# Revit family: RN 92001 Optifitt-Serra-Raccordo
name_source: partatom
category: Rohrformteile
units: mm (PartAtom-declared; Revit-internal decimal feet)

## family parameters
Arbeitsebenenbasiert = Nein
Beim Laden mit Abzugskörper schneiden = Nein
Bemaßung runder Anschluss = Durchmesser verwenden
Gemeinsam genutzt = Nein
Immer vertikal = Ja
Teiletyp = Verbindung

## types (10) — shared parameters
1.010.00.2 Blattnummer der Richtlinie = 29
1.010.00.3 Ausgabedatum (Monat) der Richtlinie = 201308
1.010.00.4 Herstellername = R. Nussbaum AG
1.010.00.5 Revisionsdatum der Datei = 20190521
1.010.00.6 Webadresse des Herstellers = http://www.nussbaum.ch
1.100.00.4 Produktbezeichnung = Versorgung
1.110.00.2 Index = 3
1.110.00.4 Produktbezeichnung = Optifitt-Serra
1.960/3L.00.8 Link (URL) = https://www.nussbaum.ch
29.700.00.4 Produktname = Optifitt-Serra-Anschlussverschraubung, mit Aussengewinde
29.700.00.5 Produktkennung = 2
29.700.00.6 Querschnittsform = 1
29.700.00.7 Nennweitensystem = DN
29.700.00.8 Nenndrucksystem = PN
29.710.02.4 Nenndruck = 16
29.710.02.5 max. zul. Überdruck [hPa] = 1600
29.710.02.7 max. zul. Dauer-Betriebsdruck [hPa] = 1600
29.710.02.9 max. zul. Dauer-Betriebstemperatur [°C] = 90
Connector Visibility = Nein
EnclosingSpace Visibility = Nein
Hersteller = R. Nussbaum AG
URL = https://www.nussbaum.ch

## per-type parameters (varying)
- DN=65: 1.800.00.3 TGA-Nummer=01900300000000000000000000000000000000000000000037000000000000000010; 1.800.00.4 Kommentarfeld=92001.30, Optifitt-Serra-Anschlussverschraubung, mit Aussengewinde, DN=65, L=70, R=2½; 1.810.00.3 Hersteller-Bestellnummer=92001.3; 1.810.00.4 DATANORM-Nummer=92001.3; 1.810.00.5 StLB-Nummer=671.121; 1.810.00.6 GTIN-Nummer=7612945036858; 29.710.02.10 Formstück-Gewicht [kg]=1.179; 29.710.02.3 Benennung=Optifitt-Serra-Anschlussverschraubung, mit Aussengewinde, DN=65, L=70, R=2½; CONNECTOR0_DIAMETER_dX_0r=65 mm; CONNECTOR0_dX_01=27 mm; CONNECTOR0_ref_dX=27 mm; CONNECTOR1_DIAMETER_dX_0r=80 mm; CONNECTOR1_dX_00=70 mm; CONNECTOR1_dX_01=87 mm; CONNECTOR1_ref_dX=70 mm; Modell=92001.3; R. Nussbaum AG 92001.24 de Visibility=Nein; R. Nussbaum AG 92001.25 de Visibility=Nein; R. Nussbaum AG 92001.26 de Visibility=Nein; R. Nussbaum AG 92001.27 de Visibility=Nein; R. Nussbaum AG 92001.28 de Visibility=Nein; R. Nussbaum AG 92001.29 de Visibility=Nein; R. Nussbaum AG 92001.30 de Visibility=Ja; R. Nussbaum AG 92001.31 de Visibility=Nein; R. Nussbaum AG 92001.74 de Visibility=Nein; R. Nussbaum AG 92001.75 de Visibility=Nein; Typenkommentare=Optifitt-Serra-Raccordo  DN=65
- DN=20: 1.800.00.3 TGA-Nummer=01900300000000000000000000000000000000000000000037000000000000000009; 1.800.00.4 Kommentarfeld=92001.75, Optifitt-Serra-Anschlussverschraubung, mit Aussengewinde, DN=20, L=37, R=¾; 1.810.00.3 Hersteller-Bestellnummer=92001.75; 1.810.00.4 DATANORM-Nummer=92001.75; 1.810.00.5 StLB-Nummer=671.114; 1.810.00.6 GTIN-Nummer=7612945036889; 29.710.02.10 Formstück-Gewicht [kg]=0.135; 29.710.02.3 Benennung=Optifitt-Serra-Anschlussverschraubung, mit Aussengewinde, DN=20, L=37, R=¾; CONNECTOR0_DIAMETER_dX_0r=20 mm; CONNECTOR0_dX_01=15 mm  [stored 0.0492126 ft]; CONNECTOR0_ref_dX=15 mm  [stored 0.0492126 ft]; CONNECTOR1_DIAMETER_dX_0r=25 mm  [stored 0.082021 ft]; CONNECTOR1_dX_00=37 mm; CONNECTOR1_dX_01=46 mm; CONNECTOR1_ref_dX=37 mm; Modell=92001.75; R. Nussbaum AG 92001.24 de Visibility=Nein; R. Nussbaum AG 92001.25 de Visibility=Nein; R. Nussbaum AG 92001.26 de Visibility=Nein; R. Nussbaum AG 92001.27 de Visibility=Nein; R. Nussbaum AG 92001.28 de Visibility=Nein; R. Nussbaum AG 92001.29 de Visibility=Nein; R. Nussbaum AG 92001.30 de Visibility=Nein; R. Nussbaum AG 92001.31 de Visibility=Nein; R. Nussbaum AG 92001.74 de Visibility=Nein; R. Nussbaum AG 92001.75 de Visibility=Ja; Typenkommentare=Optifitt-Serra-Raccordo  DN=20
- DN=15: 1.800.00.3 TGA-Nummer=01900300000000000000000000000000000000000000000037000000000000000008; 1.800.00.4 Kommentarfeld=92001.74, Optifitt-Serra-Anschlussverschraubung, mit Aussengewinde, DN=15, L=34, R=½; 1.810.00.3 Hersteller-Bestellnummer=92001.74; 1.810.00.4 DATANORM-Nummer=92001.74; 1.810.00.5 StLB-Nummer=671.113; 1.810.00.6 GTIN-Nummer=7612945036872; 29.710.02.10 Formstück-Gewicht [kg]=0.092; 29.710.02.3 Benennung=Optifitt-Serra-Anschlussverschraubung, mit Aussengewinde, DN=15, L=34, R=½; CONNECTOR0_DIAMETER_dX_0r=15 mm  [stored 0.0492126 ft]; CONNECTOR0_dX_01=13 mm; CONNECTOR0_ref_dX=13 mm; CONNECTOR1_DIAMETER_dX_0r=20 mm; CONNECTOR1_dX_00=34 mm; CONNECTOR1_dX_01=42 mm; CONNECTOR1_ref_dX=34 mm; Modell=92001.74; R. Nussbaum AG 92001.24 de Visibility=Nein; R. Nussbaum AG 92001.25 de Visibility=Nein; R. Nussbaum AG 92001.26 de Visibility=Nein; R. Nussbaum AG 92001.27 de Visibility=Nein; R. Nussbaum AG 92001.28 de Visibility=Nein; R. Nussbaum AG 92001.29 de Visibility=Nein; R. Nussbaum AG 92001.30 de Visibility=Nein; R. Nussbaum AG 92001.31 de Visibility=Nein; R. Nussbaum AG 92001.74 de Visibility=Ja; R. Nussbaum AG 92001.75 de Visibility=Nein; Typenkommentare=Optifitt-Serra-Raccordo  DN=15
- DN=50: 1.800.00.3 TGA-Nummer=01900300000000000000000000000000000000000000000037000000000000000007; 1.800.00.4 Kommentarfeld=92001.31, Optifitt-Serra-Anschlussverschraubung, mit Aussengewinde, DN=50, L=57, R=2; 1.810.00.3 Hersteller-Bestellnummer=92001.31; 1.810.00.4 DATANORM-Nummer=92001.31; 1.810.00.6 GTIN-Nummer=7612945036865; 29.710.02.10 Formstück-Gewicht [kg]=0.672; 29.710.02.3 Benennung=Optifitt-Serra-Anschlussverschraubung, mit Aussengewinde, DN=50, L=57, R=2; CONNECTOR0_DIAMETER_dX_0r=50 mm  [stored 0.164042 ft]; CONNECTOR0_dX_01=24 mm; CONNECTOR0_ref_dX=24 mm; CONNECTOR1_DIAMETER_dX_0r=50 mm  [stored 0.164042 ft]; CONNECTOR1_dX_00=57 mm  [stored 0.187008 ft]; CONNECTOR1_dX_01=71 mm; CONNECTOR1_ref_dX=57 mm  [stored 0.187008 ft]; Modell=92001.31; R. Nussbaum AG 92001.24 de Visibility=Nein; R. Nussbaum AG 92001.25 de Visibility=Nein; R. Nussbaum AG 92001.26 de Visibility=Nein; R. Nussbaum AG 92001.27 de Visibility=Nein; R. Nussbaum AG 92001.28 de Visibility=Nein; R. Nussbaum AG 92001.29 de Visibility=Nein; R. Nussbaum AG 92001.30 de Visibility=Nein; R. Nussbaum AG 92001.31 de Visibility=Ja; R. Nussbaum AG 92001.74 de Visibility=Nein; R. Nussbaum AG 92001.75 de Visibility=Nein; Typenkommentare=Optifitt-Serra-Raccordo  DN=50
- DN=3: 1.800.00.3 TGA-Nummer=01900300000000000000000000000000000000000000000037000000000000000006; 1.800.00.4 Kommentarfeld=92001.29, Optifitt-Serra-Anschlussverschraubung, mit Aussengewinde, DN=50, L=60, R=2; 1.810.00.3 Hersteller-Bestellnummer=92001.29; 1.810.00.4 DATANORM-Nummer=92001.29; 1.810.00.5 StLB-Nummer=671.118; 1.810.00.6 GTIN-Nummer=7612945036841; 29.710.02.10 Formstück-Gewicht [kg]=0.765; 29.710.02.3 Benennung=Optifitt-Serra-Anschlussverschraubung, mit Aussengewinde, DN=50, L=60, R=2; CONNECTOR0_DIAMETER_dX_0r=50 mm  [stored 0.164042 ft]; CONNECTOR0_dX_01=24 mm; CONNECTOR0_ref_dX=24 mm; CONNECTOR1_DIAMETER_dX_0r=65 mm; CONNECTOR1_dX_00=60 mm; CONNECTOR1_dX_01=75 mm; CONNECTOR1_ref_dX=60 mm; Modell=92001.29; R. Nussbaum AG 92001.24 de Visibility=Nein; R. Nussbaum AG 92001.25 de Visibility=Nein; R. Nussbaum AG 92001.26 de Visibility=Nein; R. Nussbaum AG 92001.27 de Visibility=Nein; R. Nussbaum AG 92001.28 de Visibility=Nein; R. Nussbaum AG 92001.29 de Visibility=Ja; R. Nussbaum AG 92001.30 de Visibility=Nein; R. Nussbaum AG 92001.31 de Visibility=Nein; R. Nussbaum AG 92001.74 de Visibility=Nein; R. Nussbaum AG 92001.75 de Visibility=Nein; Typenkommentare=Optifitt-Serra-Raccordo  DN=50
- DN=40: 1.800.00.3 TGA-Nummer=01900300000000000000000000000000000000000000000037000000000000000005; 1.800.00.4 Kommentarfeld=92001.28, Optifitt-Serra-Anschlussverschraubung, mit Aussengewinde, DN=40, L=48, R=1½; 1.810.00.3 Hersteller-Bestellnummer=92001.28; 1.810.00.4 DATANORM-Nummer=92001.28; 1.810.00.5 StLB-Nummer=671.117; 1.810.00.6 GTIN-Nummer=7612945036834; 29.710.02.10 Formstück-Gewicht [kg]=0.41; 29.710.02.3 Benennung=Optifitt-Serra-Anschlussverschraubung, mit Aussengewinde, DN=40, L=48, R=1½; CONNECTOR0_DIAMETER_dX_0r=40 mm; CONNECTOR0_dX_01=19 mm; CONNECTOR0_ref_dX=19 mm; CONNECTOR1_DIAMETER_dX_0r=40 mm; CONNECTOR1_dX_00=48 mm; CONNECTOR1_dX_01=60 mm; CONNECTOR1_ref_dX=48 mm; Modell=92001.28; R. Nussbaum AG 92001.24 de Visibility=Nein; R. Nussbaum AG 92001.25 de Visibility=Nein; R. Nussbaum AG 92001.26 de Visibility=Nein; R. Nussbaum AG 92001.27 de Visibility=Nein; R. Nussbaum AG 92001.28 de Visibility=Ja; R. Nussbaum AG 92001.29 de Visibility=Nein; R. Nussbaum AG 92001.30 de Visibility=Nein; R. Nussbaum AG 92001.31 de Visibility=Nein; R. Nussbaum AG 92001.74 de Visibility=Nein; R. Nussbaum AG 92001.75 de Visibility=Nein; Typenkommentare=Optifitt-Serra-Raccordo  DN=40
- DN=32: 1.800.00.3 TGA-Nummer=01900300000000000000000000000000000000000000000037000000000000000004; 1.800.00.4 Kommentarfeld=92001.27, Optifitt-Serra-Anschlussverschraubung, mit Aussengewinde, DN=32, L=46, R=1¼; 1.810.00.3 Hersteller-Bestellnummer=92001.27; 1.810.00.4 DATANORM-Nummer=92001.27; 1.810.00.5 StLB-Nummer=671.116; 1.810.00.6 GTIN-Nummer=7612945036827; 29.710.02.10 Formstück-Gewicht [kg]=0.293; 29.710.02.3 Benennung=Optifitt-Serra-Anschlussverschraubung, mit Aussengewinde, DN=32, L=46, R=1¼; CONNECTOR0_DIAMETER_dX_0r=32 mm  [stored 0.104987 ft]; CONNECTOR0_dX_01=19 mm; CONNECTOR0_ref_dX=19 mm; CONNECTOR1_DIAMETER_dX_0r=40 mm; CONNECTOR1_dX_00=46 mm; CONNECTOR1_dX_01=57 mm  [stored 0.187008 ft]; CONNECTOR1_ref_dX=46 mm; Modell=92001.27; R. Nussbaum AG 92001.24 de Visibility=Nein; R. Nussbaum AG 92001.25 de Visibility=Nein; R. Nussbaum AG 92001.26 de Visibility=Nein; R. Nussbaum AG 92001.27 de Visibility=Ja; R. Nussbaum AG 92001.28 de Visibility=Nein; R. Nussbaum AG 92001.29 de Visibility=Nein; R. Nussbaum AG 92001.30 de Visibility=Nein; R. Nussbaum AG 92001.31 de Visibility=Nein; R. Nussbaum AG 92001.74 de Visibility=Nein; R. Nussbaum AG 92001.75 de Visibility=Nein; Typenkommentare=Optifitt-Serra-Raccordo  DN=32
- DN=25: 1.800.00.3 TGA-Nummer=01900300000000000000000000000000000000000000000037000000000000000003; 1.800.00.4 Kommentarfeld=92001.26, Optifitt-Serra-Anschlussverschraubung, mit Aussengewinde, DN=25, L=42, R=1; 1.810.00.3 Hersteller-Bestellnummer=92001.26; 1.810.00.4 DATANORM-Nummer=92001.26; 1.810.00.5 StLB-Nummer=671.115; 1.810.00.6 GTIN-Nummer=7612945036810; 29.710.02.10 Formstück-Gewicht [kg]=0.215; 29.710.02.3 Benennung=Optifitt-Serra-Anschlussverschraubung, mit Aussengewinde, DN=25, L=42, R=1; CONNECTOR0_DIAMETER_dX_0r=25 mm  [stored 0.082021 ft]; CONNECTOR0_dX_01=17 mm; CONNECTOR0_ref_dX=17 mm; CONNECTOR1_DIAMETER_dX_0r=32 mm  [stored 0.104987 ft]; CONNECTOR1_dX_00=42 mm; CONNECTOR1_dX_01=52 mm; CONNECTOR1_ref_dX=42 mm; Modell=92001.26; R. Nussbaum AG 92001.24 de Visibility=Nein; R. Nussbaum AG 92001.25 de Visibility=Nein; R. Nussbaum AG 92001.26 de Visibility=Ja; R. Nussbaum AG 92001.27 de Visibility=Nein; R. Nussbaum AG 92001.28 de Visibility=Nein; R. Nussbaum AG 92001.29 de Visibility=Nein; R. Nussbaum AG 92001.30 de Visibility=Nein; R. Nussbaum AG 92001.31 de Visibility=Nein; R. Nussbaum AG 92001.74 de Visibility=Nein; R. Nussbaum AG 92001.75 de Visibility=Nein; Typenkommentare=Optifitt-Serra-Raccordo  DN=25
- DN=1: 1.800.00.3 TGA-Nummer=01900300000000000000000000000000000000000000000037000000000000000002; 1.800.00.4 Kommentarfeld=92001.25, Optifitt-Serra-Anschlussverschraubung, mit Aussengewinde, DN=20, L=37, R=¾; 1.810.00.3 Hersteller-Bestellnummer=92001.25; 1.810.00.4 DATANORM-Nummer=92001.25; 1.810.00.5 StLB-Nummer=671.114; 1.810.00.6 GTIN-Nummer=7612945036803; 29.710.02.10 Formstück-Gewicht [kg]=0.133; 29.710.02.3 Benennung=Optifitt-Serra-Anschlussverschraubung, mit Aussengewinde, DN=20, L=37, R=¾; CONNECTOR0_DIAMETER_dX_0r=20 mm; CONNECTOR0_dX_01=15 mm  [stored 0.0492126 ft]; CONNECTOR0_ref_dX=15 mm  [stored 0.0492126 ft]; CONNECTOR1_DIAMETER_dX_0r=25 mm  [stored 0.082021 ft]; CONNECTOR1_dX_00=37 mm; CONNECTOR1_dX_01=46 mm; CONNECTOR1_ref_dX=37 mm; Modell=92001.25; R. Nussbaum AG 92001.24 de Visibility=Nein; R. Nussbaum AG 92001.25 de Visibility=Ja; R. Nussbaum AG 92001.26 de Visibility=Nein; R. Nussbaum AG 92001.27 de Visibility=Nein; R. Nussbaum AG 92001.28 de Visibility=Nein; R. Nussbaum AG 92001.29 de Visibility=Nein; R. Nussbaum AG 92001.30 de Visibility=Nein; R. Nussbaum AG 92001.31 de Visibility=Nein; R. Nussbaum AG 92001.74 de Visibility=Nein; R. Nussbaum AG 92001.75 de Visibility=Nein; Typenkommentare=Optifitt-Serra-Raccordo  DN=20
- DN=2: 1.800.00.3 TGA-Nummer=01900300000000000000000000000000000000000000000037000000000000000001; 1.800.00.4 Kommentarfeld=92001.24, Optifitt-Serra-Anschlussverschraubung, mit Aussengewinde, DN=15, L=34, R=½; 1.810.00.3 Hersteller-Bestellnummer=92001.24; 1.810.00.4 DATANORM-Nummer=92001.24; 1.810.00.5 StLB-Nummer=671.113; 1.810.00.6 GTIN-Nummer=7612945036797; 29.710.02.10 Formstück-Gewicht [kg]=0.087; 29.710.02.3 Benennung=Optifitt-Serra-Anschlussverschraubung, mit Aussengewinde, DN=15, L=34, R=½; CONNECTOR0_DIAMETER_dX_0r=15 mm  [stored 0.0492126 ft]; CONNECTOR0_dX_01=13 mm; CONNECTOR0_ref_dX=13 mm; CONNECTOR1_DIAMETER_dX_0r=20 mm; CONNECTOR1_dX_00=34 mm; CONNECTOR1_dX_01=42 mm; CONNECTOR1_ref_dX=34 mm; Modell=92001.24; R. Nussbaum AG 92001.24 de Visibility=Ja; R. Nussbaum AG 92001.25 de Visibility=Nein; R. Nussbaum AG 92001.26 de Visibility=Nein; R. Nussbaum AG 92001.27 de Visibility=Nein; R. Nussbaum AG 92001.28 de Visibility=Nein; R. Nussbaum AG 92001.29 de Visibility=Nein; R. Nussbaum AG 92001.30 de Visibility=Nein; R. Nussbaum AG 92001.31 de Visibility=Nein; R. Nussbaum AG 92001.74 de Visibility=Nein; R. Nussbaum AG 92001.75 de Visibility=Nein; Typenkommentare=Optifitt-Serra-Raccordo  DN=15

note: [stored X ft] marks values corroborated as IEEE doubles in the binary element streams (Revit-internal decimal feet)

## geometry (parser evidence)
native form markers: Sweep x2
no freeform markers — native parametric forms only
